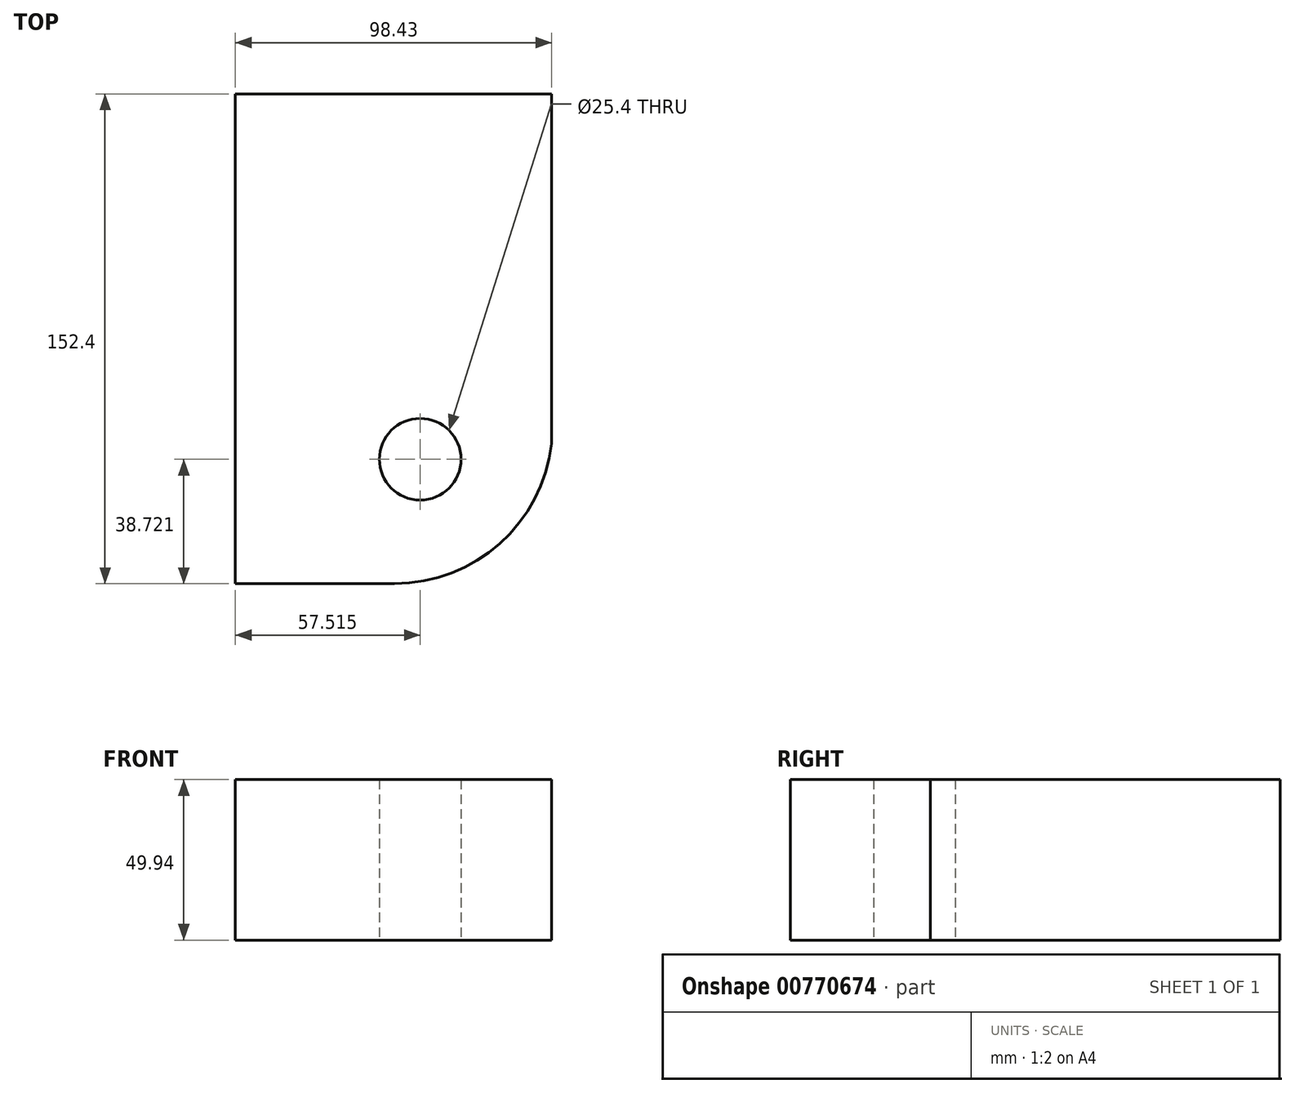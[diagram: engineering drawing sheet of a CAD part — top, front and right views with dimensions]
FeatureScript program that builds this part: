
annotation { "Feature Type Name" : "Feature", "Feature Type Description" : "" }
export const myFeature = defineFeature(function(context is Context, id is Id, definition is map)
    precondition{}
    {
        {
            var Q0;
            Q0=qCreatedBy(makeId("Front.planeOp"),FACE);
            var sketch = newSketch(context, id + "F0", { "sketchPlane" : qUnion([Q0])});
            skLineSegment(sketch, "E0.bottom", {"start": v(0, 0) * mm, "end": v(98.43, 0) * mm});
            skLineSegment(sketch, "E0.top", {"start": v(0, -49.94) * mm, "end": v(98.43, -49.94) * mm});
            skLineSegment(sketch, "E0.left", {"start": v(0, 0) * mm, "end": v(0, -49.94) * mm});
            skLineSegment(sketch, "E0.right", {"start": v(98.43, 0) * mm, "end": v(98.43, -49.94) * mm});
            skSolve(sketch);
        }
        {
            var Q0;
            Q0=makeQuery(id+"F0.imprint","IMPRINT",FACE,{"disambiguationData":[TD([[makeQuery(id+"F0.imprint","IMPRINT",EDGE,{"derivedFrom":sQuery(id+"F0.wireOp",EDGE,"E0.bottom")}),-1.0]])]});
            var Q1;
            Q1 = qSketchRegion(id + "F0", true);
            extrude(context, id + "F1", {"entities" : qUnion([Q0, Q1]), "depth" : 152.4 * mm, "offsetDistance" : 25.4 * mm});
        }
        {
            var Q0;
            Q0=makeQuery(id+"F1.opExtrude","SWEPT_FACE",FACE,{"disambiguationData":[OSD([sQuery(id+"F0.wireOp",EDGE,"E0.top")])]});
            var sketch = newSketch(context, id + "F2", { "sketchPlane" : qUnion([Q0])});
            skCircle(sketch, "E1", {"center": v(49.5, 103.13) * mm, "radius": 49.27 * mm});
            skSolve(sketch);
        }
        {
            var Q0;
            {var subQ0=sQuery(id+"F2.wireOp",EDGE,"E1");var subQ1=sQuery(id+"F0.wireOp",EDGE,"E0.top");var subQ2=makeQuery(id+"F1.opExtrude","CAP_EDGE",EDGE,{"disambiguationData":[OSD([subQ1])],"isStart":false});var subQ3=makeQuery(id+"F2.imprint","INTERSECT",VERTEX,{"derivedFrom":[subQ2,subQ0]});Q0=makeQuery(id+"F2.imprint","IMPRINT",FACE,{"disambiguationData":[TD([[makeQuery(id+"F2.imprint","IMPRINT",EDGE,{"disambiguationData":[TD([[subQ3,1.0]])],"derivedFrom":subQ0}),-1.0]])]});}
            extrude(context, id + "F3", {"entities" : qUnion([Q0]), "operationType" : NewBodyOperationType.ADD, "depth" : 25.4 * mm, "offsetDistance" : 25.4 * mm});
        }
        {
            var Q0;
            Q0=makeQuery(id+"F3.opExtrude","CAP_FACE",FACE,{"disambiguationData":[OSD([sQuery(id+"F0.wireOp",EDGE,"E0.top"),sQuery(id+"F0.wireOp",EDGE,"E0.right"),sQuery(id+"F2.wireOp",EDGE,"E1")])],"isStart":false});
            extrude(context, id + "F4", {"entities" : qUnion([Q0]), "operationType" : NewBodyOperationType.REMOVE, "oppositeDirection" : true, "depth" : 101.6 * mm, "offsetDistance" : 25.4 * mm});
        }
        {
            var Q0;
            Q0=makeQuery(id+"F1.opExtrude","SWEPT_FACE",FACE,{"disambiguationData":[OSD([sQuery(id+"F0.wireOp",EDGE,"E0.top")])]});
            var sketch = newSketch(context, id + "F5", { "sketchPlane" : qUnion([Q0])});
            skCircle(sketch, "E2", {"center": v(57.51, 113.68) * mm, "radius": 36.38 * mm});
            skSolve(sketch);
        }
        {
            var Q0;
            Q0=sQuery(id+"F5.wireOp",VERTEX,"E2.center");
            var Q1;
            Q1=makeQuery(id+"F1.opExtrude","SWEPT_BODY",BODY,{"disambiguationData":[OSD([sQuery(id+"F0.wireOp",EDGE,"E0.bottom"),sQuery(id+"F0.wireOp",EDGE,"E0.top"),sQuery(id+"F0.wireOp",EDGE,"E0.left"),sQuery(id+"F0.wireOp",EDGE,"E0.right")])]});
            hole(context, id + "F6", {"style" : HoleStyle.SIMPLE, "endStyle" : HoleEndStyle.THROUGH, "holeDiameter" : 25.4 * mm, "majorDiameter" : 6.35 * mm, "isTappedThrough" : true, "tappedDepth" : 12.7 * mm, "tapClearance" : 3, "locations" : qUnion([Q0]), "scope" : qUnion([Q1])});
        }
    });
